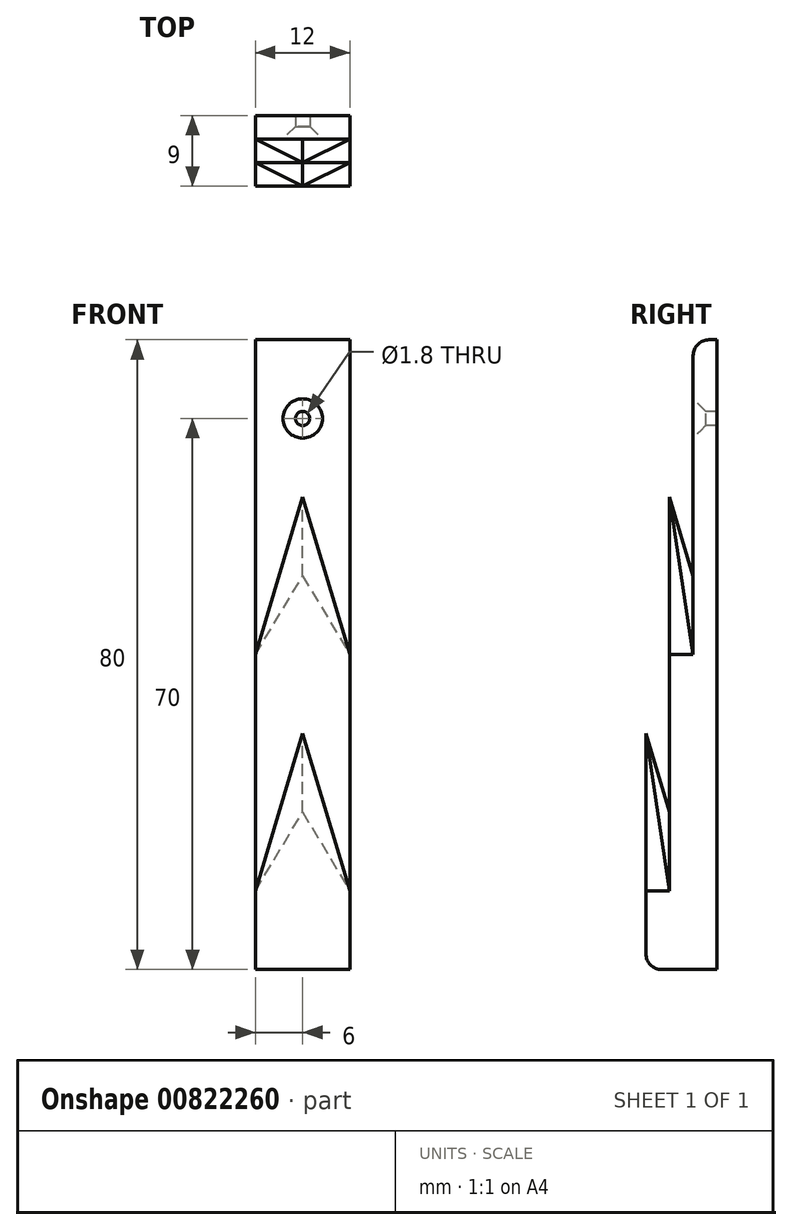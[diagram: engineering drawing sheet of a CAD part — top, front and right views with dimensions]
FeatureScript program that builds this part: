
annotation { "Feature Type Name" : "Feature", "Feature Type Description" : "" }
export const myFeature = defineFeature(function(context is Context, id is Id, definition is map)
    precondition{}
    {
        {
            var Q0;
            Q0=qCreatedBy(makeId("Right.planeOp"),FACE);
            var sketch = newSketch(context, id + "F0", { "sketchPlane" : qUnion([Q0])});
            skLineSegment(sketch, "E0", {"start": v(0, 0) * mm, "end": v(-9, 0) * mm});
            skLineSegment(sketch, "E1", {"start": v(-9, 0) * mm, "end": v(-9, 10) * mm});
            skLineSegment(sketch, "E2", {"start": v(-9, 10) * mm, "end": v(-6, 10) * mm});
            skLineSegment(sketch, "E3", {"start": v(-6, 10) * mm, "end": v(-6, 40) * mm});
            skLineSegment(sketch, "E4", {"start": v(-6, 40) * mm, "end": v(-3, 40) * mm});
            skLineSegment(sketch, "E5", {"start": v(-3, 40) * mm, "end": v(-3, 80) * mm});
            skLineSegment(sketch, "E6", {"start": v(-3, 80) * mm, "end": v(0, 80) * mm});
            skLineSegment(sketch, "E7", {"start": v(0, 80) * mm, "end": v(0, 0) * mm});
            skSolve(sketch);
        }
        {
            var Q0;
            Q0=makeQuery(id+"F0.imprint","IMPRINT",FACE,{"disambiguationData":[TD([[makeQuery(id+"F0.imprint","IMPRINT",EDGE,{"derivedFrom":sQuery(id+"F0.wireOp",EDGE,"E0")}),-1.0]])]});
            extrude(context, id + "F1", {"entities" : qUnion([Q0]), "depth" : 12 * mm, "offsetDistance" : 25 * mm});
        }
        {
            var Q0;
            Q0=makeQuery(id+"F1.opExtrude","SWEPT_FACE",FACE,{"disambiguationData":[OSD([sQuery(id+"F0.wireOp",EDGE,"E5")])]});
            var sketch = newSketch(context, id + "F2", { "sketchPlane" : qUnion([Q0])});
            skLineSegment(sketch, "E8", {"start": v(6, 80) * mm, "end": v(6, 70) * mm, "construction": true});
            skSolve(sketch);
        }
        {
            var Q0;
            Q0=sQuery(id+"F2.wireOp",VERTEX,"f9DGqX8F-WNIX-fY3L-30sl-n2NpkdaVAZb2.end");
            var Q1;
            Q1=sQuery(id+"F2.wireOp",VERTEX,"E8.end");
            var Q2;
            Q2=makeQuery(id+"F1.opExtrude","SWEPT_BODY",BODY,{"disambiguationData":[OSD([sQuery(id+"F0.wireOp",EDGE,"E0"),sQuery(id+"F0.wireOp",EDGE,"E1"),sQuery(id+"F0.wireOp",EDGE,"E2"),sQuery(id+"F0.wireOp",EDGE,"E3"),sQuery(id+"F0.wireOp",EDGE,"E4"),sQuery(id+"F0.wireOp",EDGE,"E5"),sQuery(id+"F0.wireOp",EDGE,"E6"),sQuery(id+"F0.wireOp",EDGE,"E7")])]});
            hole(context, id + "F3", {"style" : HoleStyle.C_SINK, "endStyle" : HoleEndStyle.BLIND, "holeDiameter" : 1.8 * mm, "cSinkDiameter" : 5 * mm, "cSinkAngle" : 90 * degree, "majorDiameter" : 5 * mm, "holeDepth" : 16 * mm, "isTappedThrough" : true, "tappedDepth" : 12 * mm, "tapClearance" : 3, "locations" : qUnion([Q0, Q1]), "scope" : qUnion([Q2])});
        }
        {
            var Q0;
            Q0=makeQuery(id+"F1.opExtrude","SWEPT_EDGE",EDGE,{"disambiguationData":[OSD([sQuery(id+"F0.wireOp",EDGE,"j9QddVxM-UPyw-lLxE-LeXD-Q8K2kHBCF8Sh"),sQuery(id+"F0.wireOp",EDGE,"CAPhVEik-Jkbc-wqqK-fffC-BfyIXvQkfFwp")])]});
            var Q1;
            Q1=makeQuery(id+"F1.opExtrude","SWEPT_EDGE",EDGE,{"disambiguationData":[OSD([sQuery(id+"F0.wireOp",EDGE,"j9QddVxM-UPyw-lLxE-LeXD-Q8K2kHBCF8Sh"),sQuery(id+"F0.wireOp",EDGE,"f8njTJF3-D0Yt-Y5nt-6LYo-a8GQ0gSNG2jt")])]});
            var Q2;
            Q2=makeQuery(id+"F1.opExtrude","SWEPT_EDGE",EDGE,{"disambiguationData":[OSD([sQuery(id+"F0.wireOp",EDGE,"E5"),sQuery(id+"F0.wireOp",EDGE,"E6")])]});
            var Q3;
            Q3=makeQuery(id+"F1.opExtrude","SWEPT_EDGE",EDGE,{"disambiguationData":[OSD([sQuery(id+"F0.wireOp",EDGE,"E0"),sQuery(id+"F0.wireOp",EDGE,"E1")])]});
            fillet(context, id + "F4", {"entities" : qUnion([Q0, Q1, Q2, Q3]), "radius" : 2 * mm, "tangentPropagation" : true, "allowEdgeOverflow" : false});
        }
        {
            var Q0;
            Q0=makeQuery(id+"F1.opExtrude","SWEPT_FACE",FACE,{"disambiguationData":[OSD([sQuery(id+"F0.wireOp",EDGE,"E4")])]});
            var sketch = newSketch(context, id + "F5", { "sketchPlane" : qUnion([Q0])});
            skLineSegment(sketch, "E9", {"start": v(0, -6) * mm, "end": v(0, -3) * mm});
            skLineSegment(sketch, "E10", {"start": v(0, -3) * mm, "end": v(6, 0) * mm});
            skPoint(sketch, "E10.endSnap0", {"position": v(6, -3) * mm});
            skLineSegment(sketch, "E11", {"start": v(6, 0) * mm, "end": v(12, -3) * mm});
            skLineSegment(sketch, "E12", {"start": v(12, -3) * mm, "end": v(12, -6) * mm});
            skLineSegment(sketch, "E13", {"start": v(12, -6) * mm, "end": v(0, -6) * mm});
            skSolve(sketch);
        }
        {
            var Q0;
            Q0=makeQuery(id+"F5.imprint","IMPRINT",FACE,{"disambiguationData":[TD([[makeQuery(id+"F5.imprint","IMPRINT",EDGE,{"derivedFrom":sQuery(id+"F5.wireOp",EDGE,"E9")}),-1.0]])]});
            cPlane(context, id + "F6", {"entities" : qUnion([Q0]), "cplaneType" : CPlaneType.OFFSET, "offset" : 20 * mm, "width" : 150 * mm, "height" : 150 * mm});
        }
        {
            var Q0;
            Q0=qCreatedBy(id+"F6.planeOp",FACE);
            var sketch = newSketch(context, id + "F7", { "sketchPlane" : qUnion([Q0])});
            skPoint(sketch, "E14.0", {"position": v(6, -6) * mm});
            skSolve(sketch);
        }
        {
            var Q1;
            Q1 = qSketchRegion(id + "F5", true);
            var Q2;
            Q2=sQuery(id+"F7.wireOp",VERTEX,"E14.0");
            loft(context, id + "F8", {"operationType" : NewBodyOperationType.ADD, "sheetProfilesArray" : [{ "sheetProfileEntities" : qUnion([Q1]) }, { "sheetProfileEntities" : qUnion([Q2]) }]});
        }
        {
            var Q0;
            Q0=makeQuery(id+"F1.opExtrude","SWEPT_FACE",FACE,{"disambiguationData":[OSD([sQuery(id+"F0.wireOp",EDGE,"E2")])]});
            var sketch = newSketch(context, id + "F9", { "sketchPlane" : qUnion([Q0])});
            skLineSegment(sketch, "E15", {"start": v(0, -9) * mm, "end": v(0, -6) * mm});
            skPoint(sketch, "E16.0", {"position": v(6, -3) * mm});
            skLineSegment(sketch, "E17", {"start": v(0, -6) * mm, "end": v(6, -3) * mm});
            skLineSegment(sketch, "E18", {"start": v(6, -3) * mm, "end": v(12, -6) * mm});
            skLineSegment(sketch, "E19", {"start": v(12, -6) * mm, "end": v(12, -9) * mm});
            skLineSegment(sketch, "E20", {"start": v(12, -9) * mm, "end": v(0, -9) * mm});
            skSolve(sketch);
        }
        {
            var Q0;
            Q0=makeQuery(id+"F9.imprint","IMPRINT",FACE,{"disambiguationData":[TD([[makeQuery(id+"F9.imprint","IMPRINT",EDGE,{"derivedFrom":sQuery(id+"F9.wireOp",EDGE,"E15")}),-1.0]])]});
            cPlane(context, id + "F10", {"entities" : qUnion([Q0]), "cplaneType" : CPlaneType.OFFSET, "offset" : 20 * mm, "width" : 150 * mm, "height" : 150 * mm});
        }
        {
            var Q0;
            Q0=qCreatedBy(id+"F10.planeOp",FACE);
            var sketch = newSketch(context, id + "F11", { "sketchPlane" : qUnion([Q0])});
            skPoint(sketch, "E21.0", {"position": v(6, -9) * mm});
            skSolve(sketch);
        }
        {
            var Q1;
            Q1 = qSketchRegion(id + "F9", true);
            var Q2;
            Q2=sQuery(id+"F11.wireOp",VERTEX,"E21.0");
            loft(context, id + "F12", {"operationType" : NewBodyOperationType.ADD, "sheetProfilesArray" : [{ "sheetProfileEntities" : qUnion([Q1]) }, { "sheetProfileEntities" : qUnion([Q2]) }]});
        }
    });
